# Revit family: НЕВАТОМ_Фильтр-бокс AxB FVG, версия 1
name_source: partatom
category: Арматура воздуховодов
revit_build: Autodesk Revit 2017 (Build: 20170118_1100(x64)
units: mm (PartAtom-declared; Revit-internal decimal feet)

## family parameters
Всегда вертикально = Нет
На основе рабочей плоскости = Нет
Общий = Нет
При загрузке вырезать с полостями = Нет
Размер круглого соединителя = Использовать диаметр
Тип детали = Вставляется

## types (10) — shared parameters
ADSK_Единица измерения = шт.
ADSK_Завод-изготовитель = НЕВАТОМ
ADSK_Масса_Текст = кг
ADSK_Материал наименование = Оцинкованная сталь
ADSK_Размер_Ширина = 200 мм
C = 200 мм
Nevatom_URL = https://t.me
t = 2 мм
НЕВАТОМ_Сменная кассета = FVG
Фланец = 20 мм
zero-valued in all types: ADSK_Масса

## per-type parameters (varying)
| type | A | ADSK_Наименование | ADSK_Размер_Высота | ADSK_Размер_Длина | ADSK_Расход воздуха | B |
| ФИЛЬТР-БОКС FVG-300х150–ОЦ. | 300 мм | ФИЛЬТР-БОКС FVG-300х150–ОЦ. | 150 мм | 300 мм | 400.0 м³/ч | 150 мм |
| ФИЛЬТР-БОКС FVG-400х200–ОЦ. | 400 мм | ФИЛЬТР-БОКС FVG-400х200–ОЦ. | 200 мм | 400 мм | 720.0 м³/ч | 200 мм |
| ФИЛЬТР-БОКС FVG-500х250–ОЦ. | 500 мм | ФИЛЬТР-БОКС FVG-500х250–ОЦ. | 250 мм | 500 мм | 1100.0 м³/ч | 250 мм |
| ФИЛЬТР-БОКС FVG-500х300–ОЦ. | 500 мм | ФИЛЬТР-БОКС FVG-500х300–ОЦ. | 300 мм | 500 мм | 1300.0 м³/ч | 300 мм |
| ФИЛЬТР-БОКС FVG-600х300–ОЦ. | 600 мм | ФИЛЬТР-БОКС FVG-600х300–ОЦ. | 300 мм | 600 мм | 1600.0 м³/ч | 300 мм |
| ФИЛЬТР-БОКС FVG-600х350–ОЦ. | 600 мм | ФИЛЬТР-БОКС FVG-600х350–ОЦ. | 350 мм | 600 мм | 1800.0 м³/ч | 350 мм |
| ФИЛЬТР-БОКС FVG-700х400–ОЦ. | 700 мм | ФИЛЬТР-БОКС FVG- 700х400–ОЦ. | 400 мм | 700 мм | 2500.0 м³/ч | 400 мм |
| ФИЛЬТР-БОКС FVG- 800х500–ОЦ. | 800 мм | ФИЛЬТР-БОКС FVG-800х500–ОЦ. | 500 мм | 800 мм | 3360.0 м³/ч | 500 мм |
| ФИЛЬТР-БОКС FVG- 900х500–ОЦ. | 900 мм | ФИЛЬТР-БОКС FVG-900х500–ОЦ. | 500 мм | 900 мм | 3800.0 м³/ч | 500 мм |
| ФИЛЬТР-БОКС FVG-1000х500–ОЦ. | 1000 мм | ФИЛЬТР-БОКС FVG-1000х500–ОЦ. | 500 мм | 1000 мм | 4000.0 м³/ч | 500 мм |
